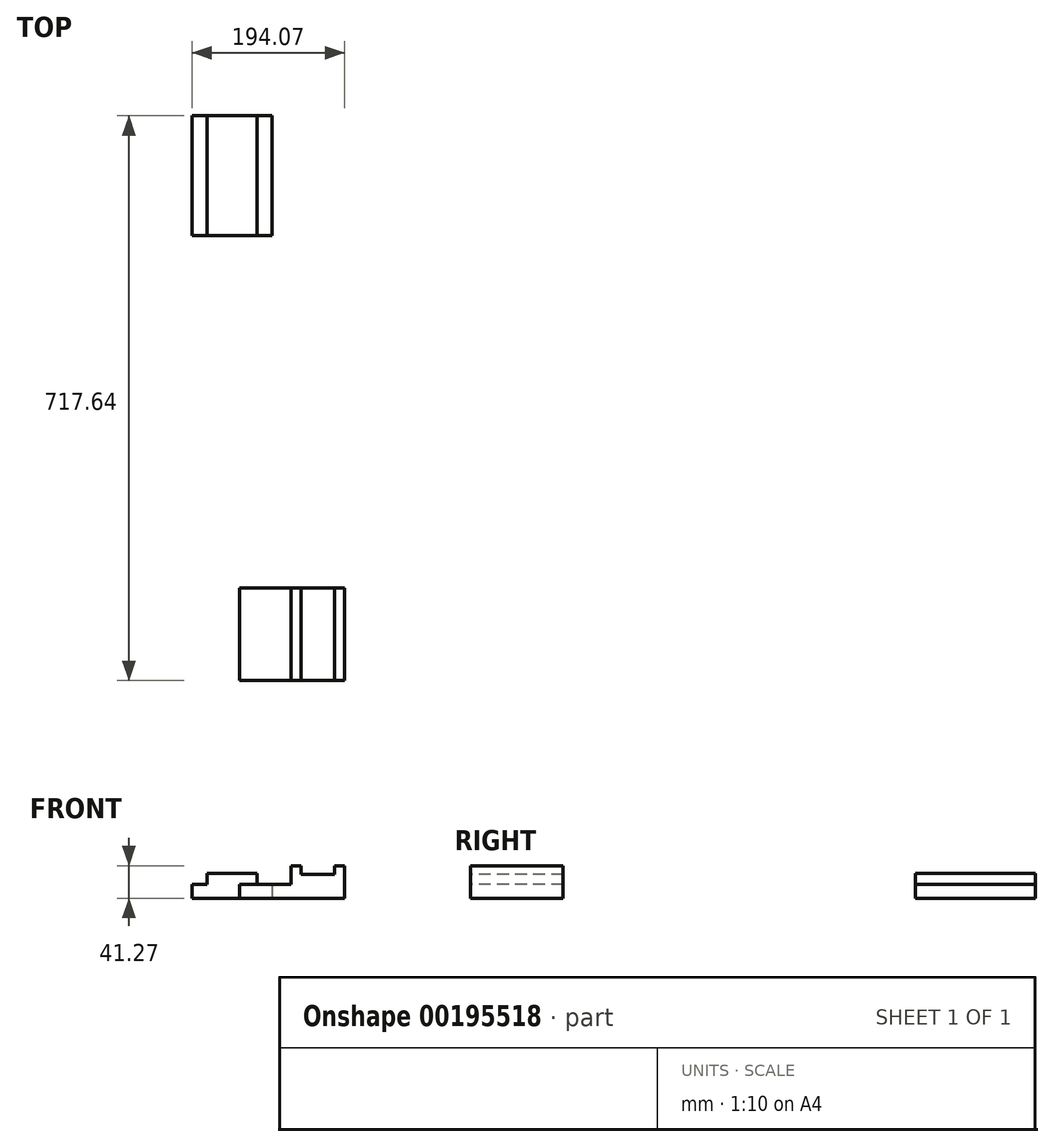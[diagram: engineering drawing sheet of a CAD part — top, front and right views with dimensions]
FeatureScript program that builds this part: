
annotation { "Feature Type Name" : "Feature", "Feature Type Description" : "" }
export const myFeature = defineFeature(function(context is Context, id is Id, definition is map)
    precondition{}
    {
        {
            var Q0;
            Q0=qCreatedBy(makeId("Top.planeOp"),FACE);
            var sketch = newSketch(context, id + "F0", { "sketchPlane" : qUnion([Q0])});
            skLineSegment(sketch, "E0.bottom", {"start": v(-79.65, 27.66) * mm, "end": v(21.95, 27.66) * mm});
            skLineSegment(sketch, "E0.top", {"start": v(-79.65, -124.74) * mm, "end": v(21.95, -124.74) * mm});
            skLineSegment(sketch, "E0.left", {"start": v(-79.65, 27.66) * mm, "end": v(-79.65, -124.74) * mm});
            skLineSegment(sketch, "E0.right", {"start": v(21.95, 27.66) * mm, "end": v(21.95, -124.74) * mm});
            skLineSegment(sketch, "E1.bottom", {"start": v(-18.93, -572.5) * mm, "end": v(114.42, -572.5) * mm});
            skLineSegment(sketch, "E1.top", {"start": v(-18.93, -689.98) * mm, "end": v(114.42, -689.98) * mm});
            skLineSegment(sketch, "E1.left", {"start": v(-18.93, -572.5) * mm, "end": v(-18.93, -689.98) * mm});
            skLineSegment(sketch, "E1.right", {"start": v(114.42, -572.5) * mm, "end": v(114.42, -689.98) * mm});
            skSolve(sketch);
        }
        {
            var Q0;
            Q0=makeQuery(id+"F0.imprint","IMPRINT",FACE,{"disambiguationData":[TD([[makeQuery(id+"F0.imprint","IMPRINT",EDGE,{"derivedFrom":sQuery(id+"F0.wireOp",EDGE,"E0.bottom")}),-1.0]])]});
            extrude(context, id + "F1", {"entities" : qUnion([Q0]), "depth" : 15.88 * mm});
        }
        {
            var Q0;
            Q0=makeQuery(id+"F1.opExtrude","CAP_FACE",FACE,{"disambiguationData":[OSD([sQuery(id+"F0.wireOp",EDGE,"E0.bottom"),sQuery(id+"F0.wireOp",EDGE,"E0.top"),sQuery(id+"F0.wireOp",EDGE,"E0.left"),sQuery(id+"F0.wireOp",EDGE,"E0.right")])],"isStart":false});
            var sketch = newSketch(context, id + "F2", { "sketchPlane" : qUnion([Q0])});
            skLineSegment(sketch, "E2", {"start": v(-79.65, 27.66) * mm, "end": v(-60.6, 27.66) * mm});
            skLineSegment(sketch, "E3", {"start": v(21.95, 27.66) * mm, "end": v(2.9, 27.66) * mm});
            skLineSegment(sketch, "E4", {"start": v(-60.6, 27.66) * mm, "end": v(-60.6, -124.74) * mm});
            skLineSegment(sketch, "E5", {"start": v(2.9, 27.66) * mm, "end": v(2.9, -124.74) * mm});
            skSolve(sketch);
        }
        {
            var Q0;
            Q0 = qSketchRegion(id + "F0", true);
            extrude(context, id + "F3", {"entities" : qUnion([Q0]), "operationType" : NewBodyOperationType.ADD, "depth" : 17.46 * mm});
        }
        {
            var Q0;
            Q0=makeQuery(id+"F3.opExtrude","CAP_FACE",FACE,{"disambiguationData":[OSD([sQuery(id+"F0.wireOp",EDGE,"E1.bottom"),sQuery(id+"F0.wireOp",EDGE,"E1.top"),sQuery(id+"F0.wireOp",EDGE,"E1.left"),sQuery(id+"F0.wireOp",EDGE,"E1.right")])],"isStart":false});
            var sketch = newSketch(context, id + "F4", { "sketchPlane" : qUnion([Q0])});
            skLineSegment(sketch, "E6", {"start": v(114.42, -572.5) * mm, "end": v(46.16, -572.5) * mm});
            skLineSegment(sketch, "E7", {"start": v(46.16, -572.5) * mm, "end": v(46.16, -689.98) * mm});
            skPoint(sketch, "E7.endSnap0", {"position": v(47.75, -689.98) * mm});
            skSolve(sketch);
        }
        {
            var Q0;
            Q0 = qSketchRegion(id + "F4", true);
            var Q1;
            Q1=makeQuery(id+"F4.imprint","IMPRINT",FACE,{"disambiguationData":[TD([[makeQuery(id+"F4.imprint","IMPRINT",EDGE,{"derivedFrom":sQuery(id+"F4.wireOp",EDGE,"E6")}),-1.0]])]});
            extrude(context, id + "F5", {"entities" : qUnion([Q0, Q1]), "operationType" : NewBodyOperationType.ADD, "depth" : 12.7 * mm});
        }
        {
            var Q0;
            Q0=makeQuery(id+"F5.opExtrude","CAP_FACE",FACE,{"disambiguationData":[OSD([sQuery(id+"F0.wireOp",EDGE,"E1.top"),sQuery(id+"F0.wireOp",EDGE,"E1.right"),sQuery(id+"F4.wireOp",EDGE,"E6"),sQuery(id+"F4.wireOp",EDGE,"E7")])],"isStart":false});
            var sketch = newSketch(context, id + "F6", { "sketchPlane" : qUnion([Q0])});
            skLineSegment(sketch, "E8", {"start": v(114.42, -572.5) * mm, "end": v(101.72, -572.5) * mm});
            skLineSegment(sketch, "E9", {"start": v(46.16, -572.5) * mm, "end": v(58.86, -572.5) * mm});
            skLineSegment(sketch, "E10", {"start": v(101.72, -572.5) * mm, "end": v(101.72, -689.98) * mm});
            skLineSegment(sketch, "E11", {"start": v(58.86, -572.5) * mm, "end": v(58.86, -689.98) * mm});
            skSolve(sketch);
        }
        {
            var Q0;
            Q0 = qSketchRegion(id + "F6", true);
            var Q1;
            Q1=makeQuery(id+"F6.imprint","IMPRINT",FACE,{"disambiguationData":[TD([[makeQuery(id+"F6.imprint","IMPRINT",EDGE,{"derivedFrom":sQuery(id+"F6.wireOp",EDGE,"E9")}),-1.0]])]});
            var Q2;
            Q2=makeQuery(id+"F6.imprint","IMPRINT",FACE,{"disambiguationData":[TD([[makeQuery(id+"F6.imprint","IMPRINT",EDGE,{"derivedFrom":sQuery(id+"F6.wireOp",EDGE,"E8")}),-1.0]])]});
            extrude(context, id + "F7", {"entities" : qUnion([Q0, Q1, Q2]), "operationType" : NewBodyOperationType.ADD, "depth" : 11.1 * mm});
        }
        {
            var Q0;
            {var subQ0=sQuery(id+"F2.wireOp",EDGE,"E4");Q0=makeQuery(id+"F2.imprint","IMPRINT",FACE,{"disambiguationData":[TD([[makeQuery(id+"F2.imprint","IMPRINT",EDGE,{"derivedFrom":subQ0}),1.0]])]});}
            extrude(context, id + "F8", {"entities" : qUnion([Q0]), "operationType" : NewBodyOperationType.ADD, "depth" : 15.88 * mm});
        }
    });
